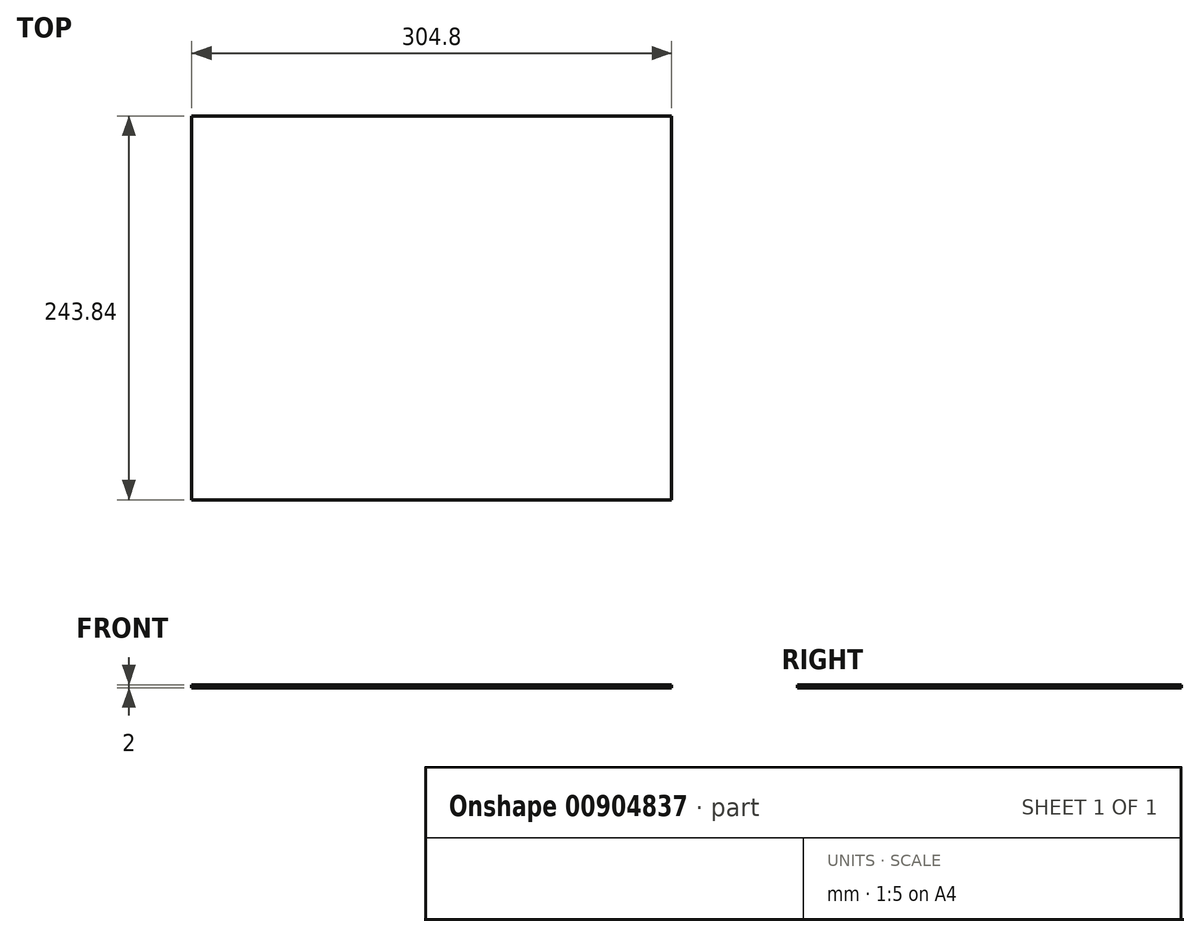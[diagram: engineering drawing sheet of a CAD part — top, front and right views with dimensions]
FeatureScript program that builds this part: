
annotation { "Feature Type Name" : "Feature", "Feature Type Description" : "" }
export const myFeature = defineFeature(function(context is Context, id is Id, definition is map)
    precondition{}
    {
        {
            var Q0;
            Q0=qCreatedBy(makeId("Top.planeOp"),FACE);
            var sketch = newSketch(context, id + "F0", { "sketchPlane" : qUnion([Q0])});
            skLineSegment(sketch, "E0.bottom", {"start": v(153.82, -121.92) * mm, "end": v(-150.98, -121.92) * mm});
            skLineSegment(sketch, "E0.top", {"start": v(153.82, 121.92) * mm, "end": v(-150.98, 121.92) * mm});
            skLineSegment(sketch, "E0.left", {"start": v(153.82, -121.92) * mm, "end": v(153.82, 121.92) * mm});
            skLineSegment(sketch, "E0.right", {"start": v(-150.98, -121.92) * mm, "end": v(-150.98, 121.92) * mm});
            skPoint(sketch, "E0.middle", {"position": v(1.42, 0) * mm});
            skSolve(sketch);
        }
        {
            var Q0;
            Q0=makeQuery(id+"F0.imprint","IMPRINT",FACE,{"disambiguationData":[TD([[makeQuery(id+"F0.imprint","IMPRINT",EDGE,{"derivedFrom":sQuery(id+"F0.wireOp",EDGE,"E0.bottom")}),-1.0]])]});
            extrude(context, id + "F1", {"entities" : qUnion([Q0]), "depth" : 2 * mm, "offsetDistance" : 25.4 * mm});
        }
    });
